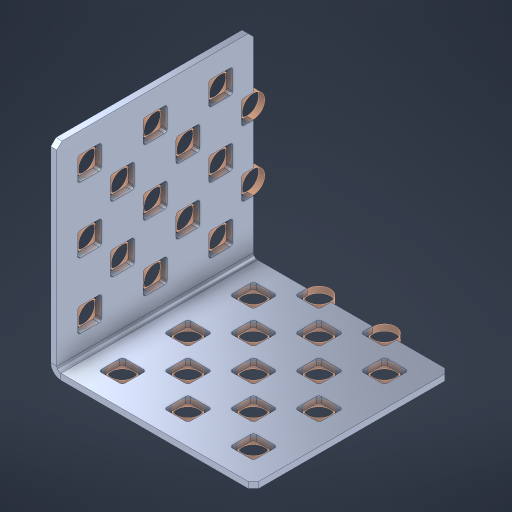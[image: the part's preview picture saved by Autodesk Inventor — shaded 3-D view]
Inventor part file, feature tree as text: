
AUTODESK INVENTOR PART (.ipt)
format: ipt  version: 2023 (Build 270158000, 158)  size: 646,656 bytes
history: native  units: in
note: dims shown in document units (in); Inventor stores cm internally (conversion verified against a paired STEP export)
features: other x36, extrude x28, sheet_metal_op x8, sketch x7, pattern_linear x3, mirror x1, chamfer x1
ambient origin geometry x8: Origin, YZ Plane, XZ Plane, XY Plane, X Axis, Y Axis, Z Axis, Center Point
bodies: Solid1 (feature_tree), Body (feature_tree)
feature tree (84):
  sheet_metal_op  "Flanges"
  sheet_metal_op  "Body Pattern"
  pattern_linear  "Center Double"  Spacing1=1.5in  [1 undecoded]
  pattern_linear  "Center Pattern"  Spacing1=0.1875in  [1 undecoded]
  other  "Arc Length"
  pattern_linear  "Notch Pattern"  Spacing1=0.0469in  [1 undecoded]
  other  "Diagonal Plane"
  mirror  "Everything Mirrored"
  chamfer  "End Chamfer"
  sketch  "Sketch1"  dims[d0=1.5in]
  other  "Plate1"
  sketch  "Sketch2"  dims[d1=1.5in]
  other  "Plate2"
  sheet_metal_op  "Bend1"
  sheet_metal_op  "Corner1"
  sketch  "Sketch8"  dims[d2=0.0469in]
  sketch  "Sketch9"  dims[d3=0.0469in]
  other  "Srf91"
  sheet_metal_op  "Body Pattern Sketch"
  other  "Srf92"
  sketch  "Sketch13"  dims[d4=0.0234in]
  sketch  "Sketch15"  dims[d5=0.0938in]
  sketch  "Sketch16"  dims[d6=0.0469in d7=1.5in d8=90.0deg d9=0.0312in d10=0.1875in d11=0.0469in d12=0.0469in d49=0.182in d50=0.02in d52=0.25in d53=0.0469in d54=0.0in d55=0.172in d56=1.0in d57=0.0in d85=0.1473in d86=0.1659in d89=0.0469in d90=0.0in d91=0.04in d92=0.0491in d95=2.5in d96=0.04in d97=0.25in d98=45.0deg d106=0.182in d107=0.02in d110=0.0469in d111=0.0in d112=0.172in d113=0.5in d114=0.0in d117=0.5in d126=0.0491in d127=0.1227in d128=0.08in d129=0.04in d130=2.5in d131=0.25in d132=1.1811in d134=0.5in d135=1.1811in d137=0.5in d140=0.5in d141=1.0in d142=0.3937in d144=0.5in d145=0.071in d146=0.7874in d148=0.5in]
  other  "Srf786"
  other  "Srf856"
  other  "Srf889"
  other  "Srf890"
  other  "Srf1275"
  other  "Srf1276"
  other  "Srf1278"
  other  "Srf1277"
  other  "Srf1285"
  other  "Srf1286"
  other  "Srf2009"
  other  "Srf2010"
  other  "Srf2011"
  other  "Srf2043"
  other  "Srf2044"
  other  "Srf2076"
  other  "Srf2077"
  other  "Srf2078"
  other  "Srf2079"
  other  "Srf2080"
  other  "Srf2081"
  other  "Srf2082"
  other  "Srf2179"
  other  "Srf2180"
  other  "Srf2181"
  other  "Srf2182"
  other  "Srf2183"
  other  "Srf2184"
  sheet_metal_op  "Body Stamp"
  sheet_metal_op  "Body Circle"
  other  "Center Stamp"
  other  "Center Circle"
  sheet_metal_op  "Notch"
  extrude  "ExtrusionSrf92"  Depth=0.0469in
  extrude  "ExtrusionSrf856"  Depth=0.182in
  extrude  "ExtrusionSrf889"  Depth=0.02in
  extrude  "ExtrusionSrf890"  Depth=0.25in
  extrude  "ExtrusionSrf1275"  Depth=0.0469in
  extrude  "ExtrusionSrf1276"  TaperAngle=0.0deg  [1 undecoded]
  extrude  "ExtrusionSrf1277"  Depth=0.5in
  extrude  "ExtrusionSrf1345"  Depth=1.0in TaperAngle=0.0deg
  extrude  "ExtrusionSrf1346"  Depth=0.5in
  extrude  "ExtrusionSrf1347"  Depth=0.5in
  extrude  "ExtrusionSrf2009"  Depth=0.0469in
  extrude  "ExtrusionSrf2010"  Depth=0.5in TaperAngle=0.0deg
  extrude  "ExtrusionSrf2011"  Depth=0.5in
  extrude  "ExtrusionSrf2043"  Depth=0.25in TaperAngle=45.0deg
  extrude  "ExtrusionSrf2044"  Depth=0.182in
  extrude  "ExtrusionSrf2076"  Depth=0.02in
  extrude  "ExtrusionSrf2077"  Depth=0.0469in
  extrude  "ExtrusionSrf2078"  TaperAngle=0.0deg  [1 undecoded]
  extrude  "ExtrusionSrf2079"  Depth=0.5in
  extrude  "ExtrusionSrf2080"  Depth=0.5in TaperAngle=0.0deg
  extrude  "ExtrusionSrf2081"  Depth=0.5in
  extrude  "ExtrusionSrf2082"  Depth=0.5in
  extrude  "ExtrusionSrf2179"  Depth=0.5in
  extrude  "ExtrusionSrf2180"  Depth=0.5in
  extrude  "ExtrusionSrf2181"  Depth=0.5in
  extrude  "ExtrusionSrf2182"  Depth=0.5in
  extrude  "ExtrusionSrf2183"  Depth=0.25in
  extrude  "ExtrusionSrf2184"  Depth=1.1811in
note: 5 required parameter values undecoded (feature->parameter linkage not recoverable at this tier; creation-order binding heuristic only, values carry confidence <= 0.55)
